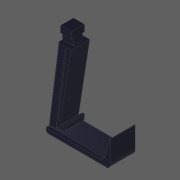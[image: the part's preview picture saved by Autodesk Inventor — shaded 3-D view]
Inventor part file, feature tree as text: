
AUTODESK INVENTOR PART (.ipt)
format: ipt  version: 2020 (Build 240168000, 168)  size: 258,048 bytes
history: native  units: in
note: dims shown in document units (in); Inventor stores cm internally (conversion verified against a paired STEP export)
features: fillet x5, other x3, extrude x3
ambient origin geometry x8: Origin, YZ Plane, XZ Plane, XY Plane, X Axis, Y Axis, Z Axis, Center Point
bodies: Solid1 (feature_tree)
feature tree (11):
  other  "Neck Start Plane"
  other  "Arm Profile"
  extrude  "Main Arm"  Depth=0.0039in
  extrude  "Pincher"  Depth=1.0386in
  extrude  "Neck"  Depth=0.7283in
  fillet  "Spring Hook Fillet"  Radius=0.1181in
  fillet  "Spring Attachment Fillet"  [1 undecoded]
  fillet  "Soft Edges"  Radius=0.195in
  fillet  "Pincher Fillet 1"  Radius=0.0197in
  fillet  "Pincher Fillet 2"  Radius=0.0394in
  other  "Neck Sketch"
note: 1 required parameter value undecoded (feature->parameter linkage not recoverable at this tier; creation-order binding heuristic only, values carry confidence <= 0.55)
